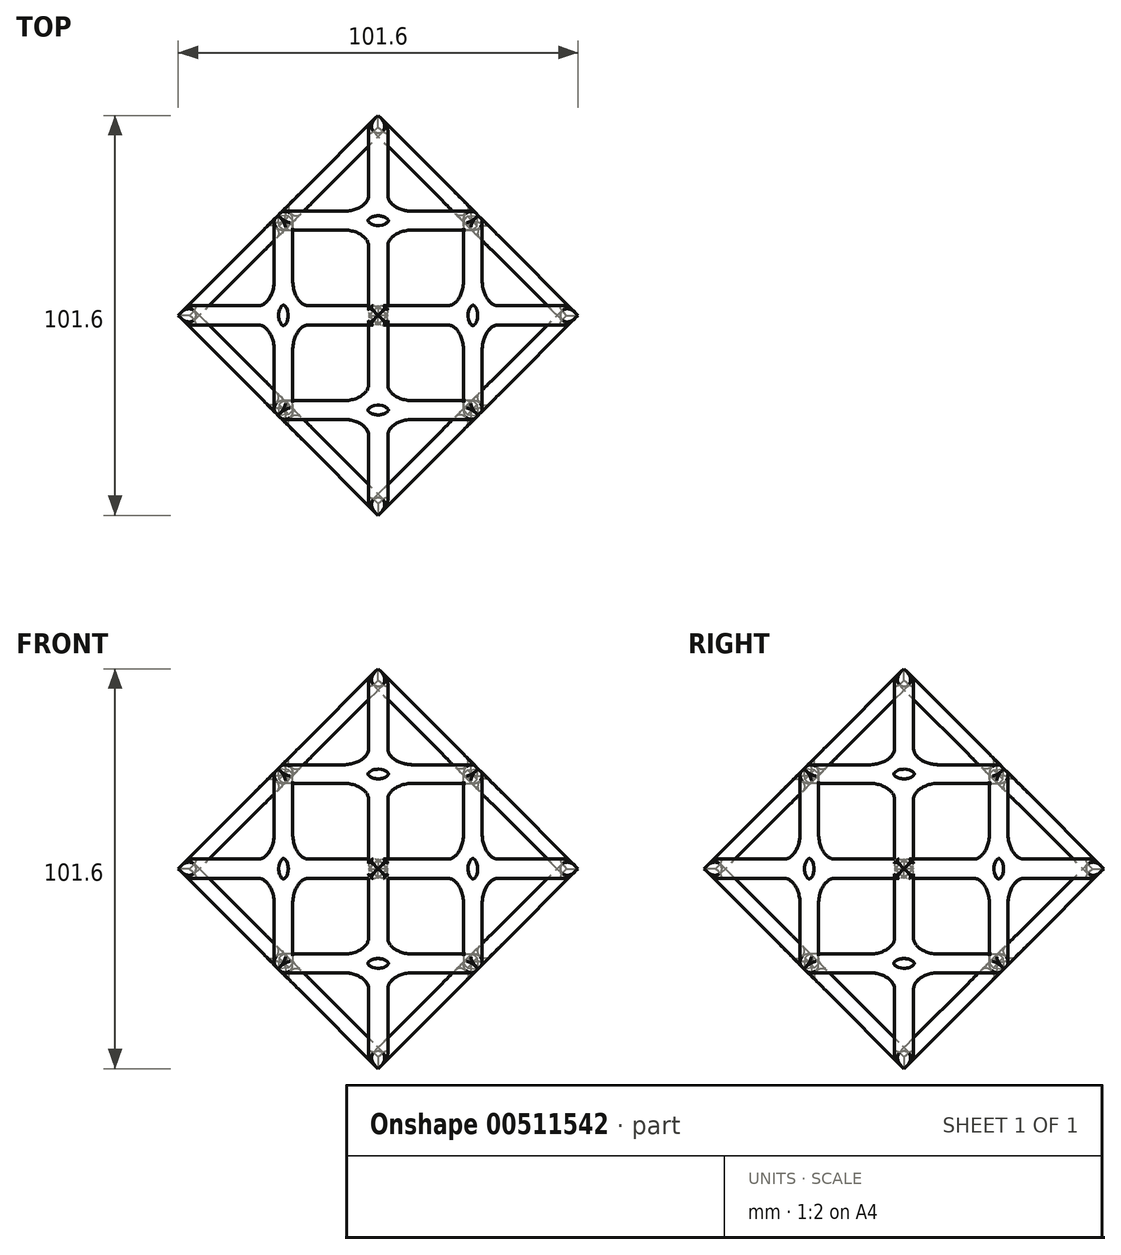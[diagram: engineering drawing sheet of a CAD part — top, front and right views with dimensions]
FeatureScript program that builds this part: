
annotation { "Feature Type Name" : "Feature", "Feature Type Description" : "" }
export const myFeature = defineFeature(function(context is Context, id is Id, definition is map)
    precondition{}
    {
        {
            var Q0;
            Q0=qCreatedBy(makeId("Right.planeOp"),FACE);
            cPlane(context, id + "F0", {"entities" : qUnion([Q0]), "cplaneType" : CPlaneType.OFFSET, "offset" : 25.4 * mm, "width" : 152.4 * mm, "height" : 152.4 * mm});
        }
        {
            var Q0;
            Q0=qCreatedBy(makeId("Right.planeOp"),FACE);
            cPlane(context, id + "F1", {"entities" : qUnion([Q0]), "cplaneType" : CPlaneType.OFFSET, "offset" : 25.4 * mm, "oppositeDirection" : true, "width" : 152.4 * mm, "height" : 152.4 * mm});
        }
        {
            var Q0;
            Q0=qCreatedBy(makeId("Right.planeOp"),FACE);
            var sketch = newSketch(context, id + "F2", { "sketchPlane" : qUnion([Q0])});
            skPoint(sketch, "E0", {"position": v(0, 50.8) * mm});
            skPoint(sketch, "E1", {"position": v(-50.8, 0) * mm});
            skPoint(sketch, "E2", {"position": v(0, -50.8) * mm});
            skPoint(sketch, "E3", {"position": v(50.8, 0) * mm});
            skSolve(sketch);
        }
        {
            var Q0;
            Q0=qCreatedBy(id+"F0.planeOp",FACE);
            var sketch = newSketch(context, id + "F3", { "sketchPlane" : qUnion([Q0])});
            skPoint(sketch, "E4", {"position": v(25.4, 25.4) * mm});
            skPoint(sketch, "E5", {"position": v(25.4, -25.4) * mm});
            skPoint(sketch, "E6", {"position": v(-25.4, -25.4) * mm});
            skPoint(sketch, "E7", {"position": v(-25.4, 25.4) * mm});
            skSolve(sketch);
        }
        {
            var Q0;
            Q0=qCreatedBy(id+"F1.planeOp",FACE);
            var sketch = newSketch(context, id + "F4", { "sketchPlane" : qUnion([Q0])});
            skPoint(sketch, "E8", {"position": v(-25.4, 25.4) * mm});
            skPoint(sketch, "E9", {"position": v(25.4, 25.4) * mm});
            skPoint(sketch, "E10", {"position": v(25.4, -25.4) * mm});
            skPoint(sketch, "E11", {"position": v(-25.4, -25.4) * mm});
            skSolve(sketch);
        }
        {
            var Q0;
            Q0=sQuery(id+"F4.wireOp",VERTEX,"E8");
            var Q1;
            Q1=sQuery(id+"F2.wireOp",VERTEX,"E0");
            var Q2;
            Q2=sQuery(id+"F3.wireOp",VERTEX,"E7");
            cPlane(context, id + "F5", {"entities" : qUnion([Q0, Q1, Q2]), "cplaneType" : CPlaneType.THREE_POINT, "offset" : 25.4 * mm, "width" : 152.4 * mm, "height" : 152.4 * mm});
        }
        {
            var Q0;
            Q0=qCreatedBy(id+"F5.planeOp",FACE);
            var sketch = newSketch(context, id + "F6", { "sketchPlane" : qUnion([Q0])});
            skLineSegment(sketch, "E12", {"start": v(-25.4, 0) * mm, "end": v(-23.6, 2.54) * mm});
            skLineSegment(sketch, "E13", {"start": v(0, 35.92) * mm, "end": v(2.54, 32.33) * mm});
            skLineSegment(sketch, "E14", {"start": v(25.4, 0) * mm, "end": v(23.6, -2.54) * mm});
            skLineSegment(sketch, "E15", {"start": v(0, -35.92) * mm, "end": v(-2.54, -32.33) * mm});
            skLineSegment(sketch, "E16", {"start": v(-23.6, 2.54) * mm, "end": v(-8.89, 2.54) * mm});
            skLineSegment(sketch, "E17", {"start": v(-2.54, 8.89) * mm, "end": v(-2.54, 32.33) * mm});
            skLineSegment(sketch, "E18", {"start": v(2.54, 32.33) * mm, "end": v(2.54, 8.89) * mm});
            skLineSegment(sketch, "E19", {"start": v(8.9, 2.54) * mm, "end": v(23.6, 2.54) * mm});
            skLineSegment(sketch, "E20", {"start": v(23.6, -2.54) * mm, "end": v(8.9, -2.54) * mm});
            skLineSegment(sketch, "E21", {"start": v(2.54, -8.9) * mm, "end": v(2.54, -32.33) * mm});
            skLineSegment(sketch, "E22", {"start": v(-23.6, -2.54) * mm, "end": v(-8.9, -2.54) * mm});
            skLineSegment(sketch, "E23", {"start": v(-2.54, -8.89) * mm, "end": v(-2.54, -32.33) * mm});
            skLineSegment(sketch, "E24.trimOffspring", {"start": v(23.6, 2.54) * mm, "end": v(25.4, 0) * mm});
            skLineSegment(sketch, "E25.trimOffspring", {"start": v(-2.54, 32.33) * mm, "end": v(0, 35.92) * mm});
            skLineSegment(sketch, "E26.trimOffspring", {"start": v(-23.6, -2.54) * mm, "end": v(-25.4, 0) * mm});
            skLineSegment(sketch, "E27.trimOffspring", {"start": v(2.54, -32.33) * mm, "end": v(0, -35.92) * mm});
            skPoint(sketch, "E28.visualSharp", {"position": v(-2.54, 2.54) * mm});
            skArc(sketch, "E28.filletArc", {"start": v(-8.89, 2.54) * mm, "mid": v(-4.4, 4.4) * mm, "end": v(-2.54, 8.89) * mm});
            skPoint(sketch, "E29.visualSharp", {"position": v(2.54, 2.54) * mm});
            skArc(sketch, "E29.filletArc", {"start": v(2.54, 8.89) * mm, "mid": v(4.4, 4.4) * mm, "end": v(8.9, 2.54) * mm});
            skPoint(sketch, "E30.visualSharp", {"position": v(2.54, -2.54) * mm});
            skArc(sketch, "E30.filletArc", {"start": v(8.9, -2.54) * mm, "mid": v(4.4, -4.4) * mm, "end": v(2.54, -8.9) * mm});
            skPoint(sketch, "E31.visualSharp", {"position": v(-2.54, -2.54) * mm});
            skArc(sketch, "E31.filletArc", {"start": v(-2.54, -8.89) * mm, "mid": v(-4.4, -4.4) * mm, "end": v(-8.9, -2.54) * mm});
            skCircle(sketch, "E32", {"center": v(0, 0) * mm, "radius": 2.54 * mm});
            skSolve(sketch);
        }
        {
            var Q0;
            Q0=makeQuery(id+"F6.imprint","IMPRINT",FACE,{"disambiguationData":[TD([[makeQuery(id+"F6.imprint","IMPRINT",EDGE,{"derivedFrom":sQuery(id+"F6.wireOp",EDGE,"E12")}),-1.0]])]});
            extrude(context, id + "F7", {"entities" : qUnion([Q0]), "oppositeDirection" : true, "depth" : 3.8 * mm, "hasDraft" : true, "draftAngle" : 3 * degree, "draftPullDirection" : true});
        }
        {
            var Q0;
            Q0=makeQuery(id+"F7.opExtrude","CAP_EDGE",EDGE,{"disambiguationData":[OSD([sQuery(id+"F6.wireOp",EDGE,"E31.filletArc")])],"isStart":true});
            var Q1;
            Q1=makeQuery(id+"F7.opExtrude","CAP_EDGE",EDGE,{"disambiguationData":[OSD([sQuery(id+"F6.wireOp",EDGE,"E32")])],"isStart":true});
            var Q2;
            Q2=makeQuery(id+"F7.opExtrude","CAP_EDGE",EDGE,{"disambiguationData":[OSD([sQuery(id+"F6.wireOp",EDGE,"E30.filletArc")])],"isStart":true});
            var Q3;
            Q3=makeQuery(id+"F7.opExtrude","CAP_EDGE",EDGE,{"disambiguationData":[OSD([sQuery(id+"F6.wireOp",EDGE,"E29.filletArc")])],"isStart":true});
            var Q4;
            Q4=makeQuery(id+"F7.opExtrude","CAP_EDGE",EDGE,{"disambiguationData":[OSD([sQuery(id+"F6.wireOp",EDGE,"E28.filletArc")])],"isStart":true});
            var Q5;
            Q5=makeQuery(id+"F7.opExtrude","CAP_EDGE",EDGE,{"disambiguationData":[OSD([sQuery(id+"F6.wireOp",EDGE,"E29.filletArc")])],"isStart":false});
            var Q6;
            Q6=makeQuery(id+"F7.opExtrude","CAP_EDGE",EDGE,{"disambiguationData":[OSD([sQuery(id+"F6.wireOp",EDGE,"E30.filletArc")])],"isStart":false});
            var Q7;
            Q7=makeQuery(id+"F7.opExtrude","CAP_EDGE",EDGE,{"disambiguationData":[OSD([sQuery(id+"F6.wireOp",EDGE,"E31.filletArc")])],"isStart":false});
            var Q8;
            Q8=makeQuery(id+"F7.opExtrude","CAP_EDGE",EDGE,{"disambiguationData":[OSD([sQuery(id+"F6.wireOp",EDGE,"E28.filletArc")])],"isStart":false});
            var Q9;
            Q9=makeQuery(id+"F7.opExtrude","CAP_EDGE",EDGE,{"disambiguationData":[OSD([sQuery(id+"F6.wireOp",EDGE,"E32")])],"isStart":false});
            fillet(context, id + "F8", {"entities" : qUnion([Q0, Q1, Q2, Q3, Q4, Q5, Q6, Q7, Q8, Q9]), "radius" : 1.71 * mm, "tangentPropagation" : true, "allowEdgeOverflow" : false});
        }
        {
            var Q0;
            Q0=qCreatedBy(makeId("Front.planeOp"),FACE);
            var sketch = newSketch(context, id + "F9", { "sketchPlane" : qUnion([Q0])});
            skLineSegment(sketch, "E33", {"start": v(0, 50.8) * mm, "end": v(0, -50.8) * mm, "construction": true});
            skSolve(sketch);
        }
        {
            var Q0;
            Q0=makeQuery(id+"F7.opExtrude","SWEPT_BODY",BODY,{"disambiguationData":[OSD([sQuery(id+"F6.wireOp",EDGE,"E12"),sQuery(id+"F6.wireOp",EDGE,"E13"),sQuery(id+"F6.wireOp",EDGE,"E14"),sQuery(id+"F6.wireOp",EDGE,"E15")])]});
            var Q1;
            Q1=sQuery(id+"F9.wireOp",EDGE,"E33");
            circularPattern(context, id + "F10", {"entities" : qUnion([Q0]), "axis" : qUnion([Q1]), "angle" : 360 * degree, "instanceCount" : 4, "equalSpace" : true});
        }
        {
            var Q0;
            Q0=qCreatedBy(makeId("Right.planeOp"),FACE);
            var sketch = newSketch(context, id + "F11", { "sketchPlane" : qUnion([Q0])});
            skLineSegment(sketch, "E34", {"start": v(50.8, 0) * mm, "end": v(-50.8, 0) * mm, "construction": true});
            skSolve(sketch);
        }
        {
            var Q0;
            Q0=makeQuery(id+"F10.opPattern","COPY",BODY,{"derivedFrom":makeQuery(id+"F7.opExtrude","SWEPT_BODY",BODY,{"disambiguationData":[OSD([sQuery(id+"F6.wireOp",EDGE,"E12"),sQuery(id+"F6.wireOp",EDGE,"E13"),sQuery(id+"F6.wireOp",EDGE,"E14"),sQuery(id+"F6.wireOp",EDGE,"E15")])]}),"instanceName":"2"});
            var Q1;
            Q1=sQuery(id+"F11.wireOp",EDGE,"E34");
            circularPattern(context, id + "F12", {"entities" : qUnion([Q0]), "axis" : qUnion([Q1]), "angle" : 360 * degree, "instanceCount" : 4, "equalSpace" : true});
        }
        {
            var Q0;
            Q0=makeQuery(id+"F7.opExtrude","SWEPT_BODY",BODY,{"disambiguationData":[OSD([sQuery(id+"F6.wireOp",EDGE,"E12"),sQuery(id+"F6.wireOp",EDGE,"E13"),sQuery(id+"F6.wireOp",EDGE,"E14"),sQuery(id+"F6.wireOp",EDGE,"E15")])]});
            var Q1;
            Q1=sQuery(id+"F11.wireOp",EDGE,"E34");
            circularPattern(context, id + "F13", {"entities" : qUnion([Q0]), "axis" : qUnion([Q1]), "angle" : 360 * degree, "instanceCount" : 4, "equalSpace" : true});
        }
        {
            var Q0;
            Q0=qCreatedBy(makeId("Front.planeOp"),FACE);
            var sketch = newSketch(context, id + "F14", { "sketchPlane" : qUnion([Q0])});
            skLineSegment(sketch, "E35", {"start": v(0, 50.8) * mm, "end": v(0, -50.8) * mm, "construction": true});
            skSolve(sketch);
        }
        {
            var Q0;
            Q0=makeQuery(id+"F12.opPattern","COPY",BODY,{"derivedFrom":makeQuery(id+"F10.opPattern","COPY",BODY,{"derivedFrom":makeQuery(id+"F7.opExtrude","SWEPT_BODY",BODY,{"disambiguationData":[OSD([sQuery(id+"F6.wireOp",EDGE,"E12"),sQuery(id+"F6.wireOp",EDGE,"E13"),sQuery(id+"F6.wireOp",EDGE,"E14"),sQuery(id+"F6.wireOp",EDGE,"E15")])]}),"instanceName":"2"}),"instanceName":"2"});
            var Q1;
            Q1=sQuery(id+"F14.wireOp",EDGE,"E35");
            circularPattern(context, id + "F15", {"entities" : qUnion([Q0]), "axis" : qUnion([Q1]), "angle" : 90 * degree, "instanceCount" : 2, "equalSpace" : true});
        }
        {
            var Q0;
            Q0=makeQuery(id+"F12.opPattern","COPY",BODY,{"derivedFrom":makeQuery(id+"F10.opPattern","COPY",BODY,{"derivedFrom":makeQuery(id+"F7.opExtrude","SWEPT_BODY",BODY,{"disambiguationData":[OSD([sQuery(id+"F6.wireOp",EDGE,"E12"),sQuery(id+"F6.wireOp",EDGE,"E13"),sQuery(id+"F6.wireOp",EDGE,"E14"),sQuery(id+"F6.wireOp",EDGE,"E15")])]}),"instanceName":"2"}),"instanceName":"2"});
            var Q1;
            Q1=sQuery(id+"F14.wireOp",EDGE,"E35");
            circularPattern(context, id + "F16", {"entities" : qUnion([Q0]), "axis" : qUnion([Q1]), "angle" : 90 * degree, "instanceCount" : 2, "oppositeDirection" : true, "equalSpace" : true});
        }
    });
